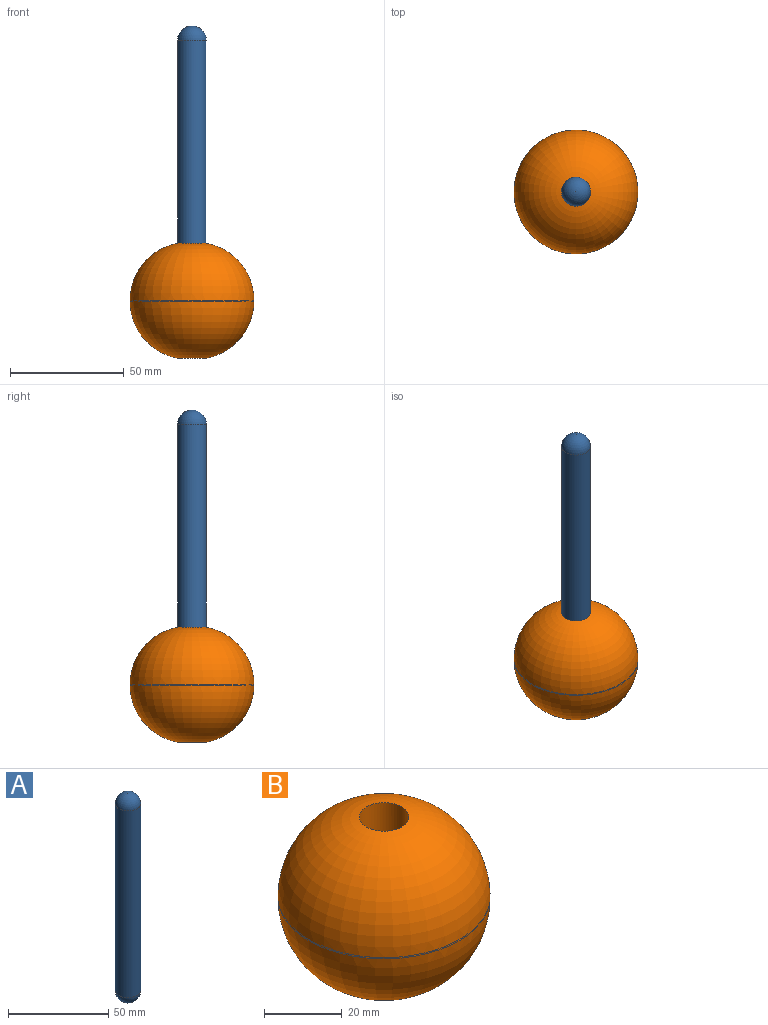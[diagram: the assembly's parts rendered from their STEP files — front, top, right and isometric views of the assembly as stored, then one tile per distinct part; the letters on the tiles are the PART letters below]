
ASSEMBLY  parts=2 mates=1
PART A: 3 faces, bbox 12.7x12.7x127 mm
  f0: cylinder r=6.35mm len=114.3mm, axis (0,0,-1), area 4560.4mm2, adj f1,f2
  f1: sphere r=6.35mm, area 253.4mm2, adj f0
  f2: sphere r=6.35mm, area 253.4mm2, adj f0
PART B: 4 faces, bbox 54.5x54.5x50.4 mm
  f0: torus R=1.85mm, axis (0,0,1), area 4401.5mm2, adj f1,f2
  f1: cylinder r=6.35mm len=50.4mm, axis (0,0,-1), area 2010.8mm2, adj f0,f3
  f2: cylinder r=27.25mm len=54.51mm, axis (0,0,1), area 68.7mm2, adj f0,f3
  f3: torus R=1.85mm, axis (0,0,-1), area 4401.5mm2, adj f1,f2
PLACE A t=(-33.97,21.27,-48.44)mm
PLACE B t=(0,0,-42.09)mm
MATE fastened A.f0 <-> B.f0  axis (0,0,1) through (-12.24,15.97,-42.09)mm
